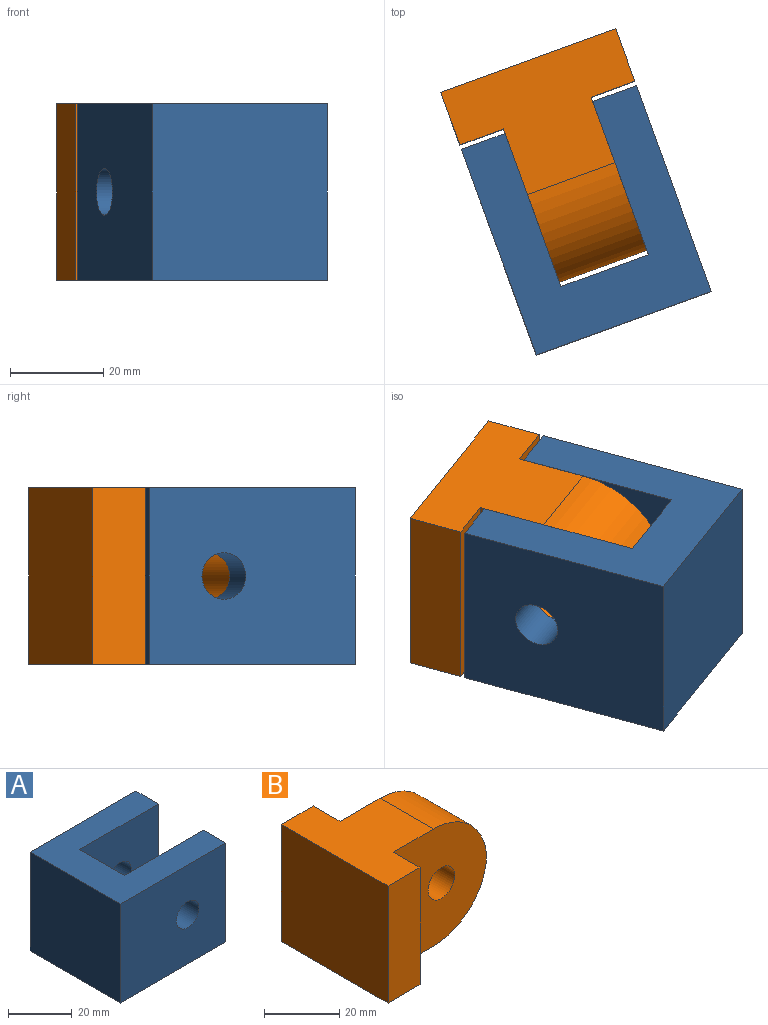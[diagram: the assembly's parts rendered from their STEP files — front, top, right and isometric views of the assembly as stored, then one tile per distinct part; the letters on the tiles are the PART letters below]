
ASSEMBLY  parts=2 mates=1
PART A: 12 faces, bbox 47x40x38 mm
  f0: plane 38x10mm, normal (1,0,0), area 380mm2, adj f1,f4,f7,f9
  f1: plane 47x40mm, normal (0,0,1), area 1180mm2, adj f0,f3,f5,f7,f8,f9,f10,f11
  f2: cylinder r=5mm len=10mm, axis (0,1,0), area 314.2mm2, adj f8,f10
  f3: plane 40x38mm, normal (-1,0,0), area 1520mm2, adj f1,f4,f7,f8
  f4: plane 47x40mm, normal (0,0,-1), area 1180mm2, adj f0,f3,f5,f7,f8,f9,f10,f11
  f5: plane 38x10mm, normal (1,0,0), area 380mm2, adj f1,f4,f8,f10
  f6: cylinder r=5mm len=10mm, axis (0,1,0), area 314.2mm2, adj f7,f9
  f7: plane 47x38mm, normal (0,-1,0), area 1707.5mm2, adj f0,f1,f3,f4,f6
  f8: plane 47x38mm, normal (0,1,0), area 1707.5mm2, adj f1,f2,f3,f4,f5
  f9: plane 38x35mm, normal (0,1,0), area 1251.5mm2, adj f0,f1,f4,f6,f11
  f10: plane 38x35mm, normal (0,-1,0), area 1251.5mm2, adj f1,f2,f4,f5,f11
  f11: plane 38x20mm, normal (1,0,0), area 760mm2, adj f1,f4,f9,f10
PART B: 12 faces, bbox 47x40x38 mm
  f0: plane 40x27mm, normal (0,0,-1), area 780mm2, adj f2,f3,f4,f5,f6,f7,f8,f11
  f1: plane 40x27mm, normal (0,0,1), area 780mm2, adj f2,f3,f4,f5,f6,f7,f8,f10
  f2: plane 38x12mm, normal (0,-1,0), area 456mm2, adj f0,f1,f4,f6
  f3: plane 38x12mm, normal (0,1,0), area 456mm2, adj f0,f1,f4,f8
  f4: plane 40x38mm, normal (-1,0,0), area 1520mm2, adj f0,f1,f2,f3
  f5: plane 38x34.98mm, normal (0,-1,0), area 1079.8mm2, adj f0,f1,f6,f9,f10,f11
  f6: plane 38x10mm, normal (1,0,0), area 380mm2, adj f0,f1,f2,f5
  f7: plane 38x34.98mm, normal (0,1,0), area 1079.8mm2, adj f0,f1,f8,f9,f10,f11
  f8: plane 38x10mm, normal (1,0,0), area 380mm2, adj f0,f1,f3,f7
  f9: cylinder r=5mm len=20mm, axis (0,1,0), area 628.3mm2, adj f5,f7
  f10: cylinder r=20mm len=20mm, axis (0,-1,0), area 608.3mm2, adj f1,f5,f7,f11
  f11: cylinder r=20mm len=20mm, axis (0,1,0), area 608.3mm2, adj f0,f5,f7,f10
PLACE A rot(axis=(-0.57,-0.82,0),180deg) t=(160.65,54.58,-30.36)mm
PLACE B rot(axis=(0,0,-1),70deg) t=(140.13,110.96,-68.36)mm
MATE revolute B.f9 <-> A.f2  axis (0.94,0.34,0) through (140.99,79.35,-49.36)mm
